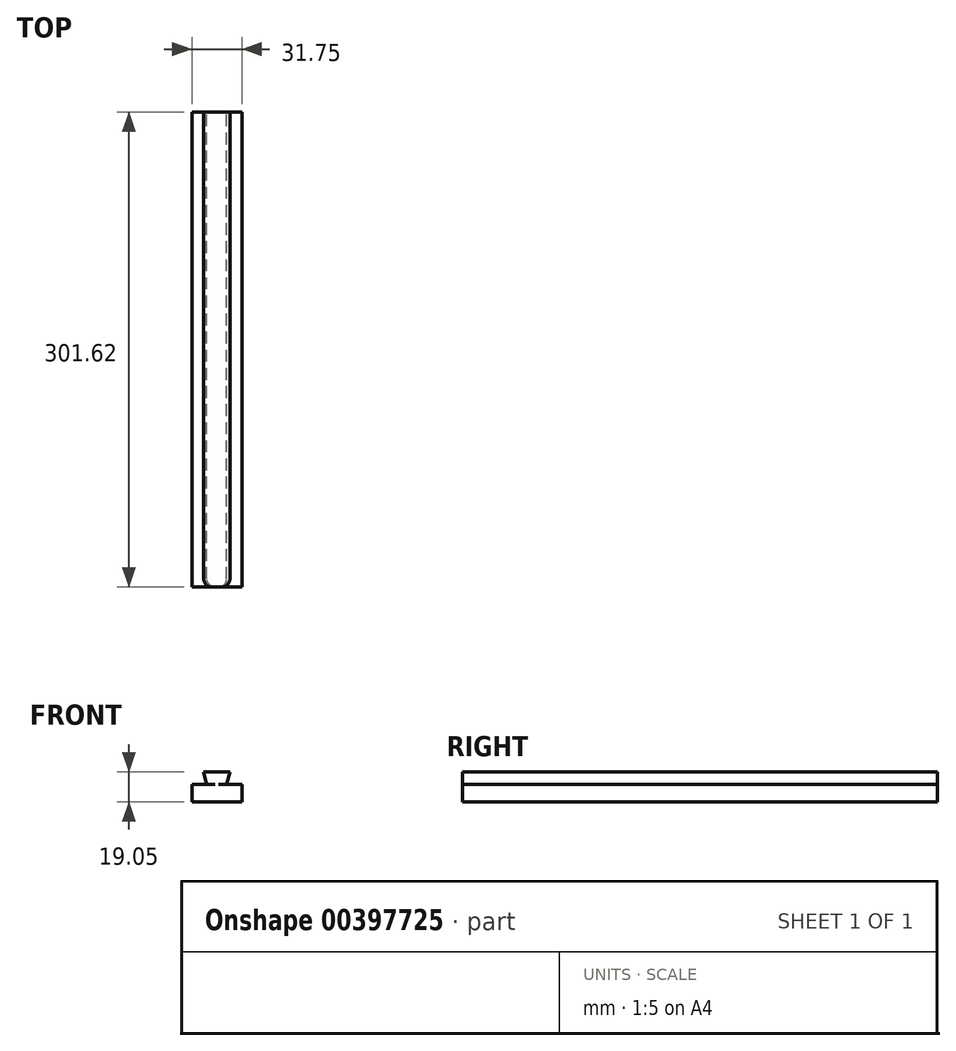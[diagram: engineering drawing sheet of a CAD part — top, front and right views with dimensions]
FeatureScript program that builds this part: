
annotation { "Feature Type Name" : "Feature", "Feature Type Description" : "" }
export const myFeature = defineFeature(function(context is Context, id is Id, definition is map)
    precondition{}
    {
        {
            var Q0;
            Q0=qCreatedBy(makeId("Front.planeOp"),FACE);
            var sketch = newSketch(context, id + "F0", { "sketchPlane" : qUnion([Q0])});
            skLineSegment(sketch, "E0.bottom", {"start": v(0, 0) * mm, "end": v(31.75, 0) * mm});
            skLineSegment(sketch, "E0.top", {"start": v(7.55, 19.05) * mm, "end": v(24.2, 19.05) * mm});
            skLineSegment(sketch, "E0.left", {"start": v(0, 0) * mm, "end": v(0, 11.11) * mm});
            skLineSegment(sketch, "E0.right", {"start": v(31.75, 0) * mm, "end": v(31.75, 11.11) * mm});
            skLineSegment(sketch, "E1", {"start": v(7.55, 19.05) * mm, "end": v(9.52, 11.11) * mm});
            skLineSegment(sketch, "E2", {"start": v(9.52, 11.11) * mm, "end": v(0, 11.11) * mm});
            skLineSegment(sketch, "E3", {"start": v(24.2, 19.05) * mm, "end": v(22.23, 11.11) * mm});
            skLineSegment(sketch, "E4", {"start": v(22.23, 11.11) * mm, "end": v(31.75, 11.11) * mm});
            skLineSegment(sketch, "E5", {"start": v(9.52, 11.11) * mm, "end": v(22.23, 11.11) * mm, "construction": true});
            skSolve(sketch);
        }
        {
            var Q0;
            Q0=makeQuery(id+"F0.imprint","IMPRINT",FACE,{"disambiguationData":[TD([[makeQuery(id+"F0.imprint","IMPRINT",EDGE,{"derivedFrom":sQuery(id+"F0.wireOp",EDGE,"E0.bottom")}),1.0]])]});
            extrude(context, id + "F1", {"entities" : qUnion([Q0]), "depth" : 301.62 * mm});
        }
        {
            var Q0;
            Q0=makeQuery(id+"F1.opExtrude","CAP_EDGE",EDGE,{"disambiguationData":[OSD([sQuery(id+"F0.wireOp",EDGE,"E3")])],"isStart":false});
            var Q1;
            Q1=makeQuery(id+"F1.opExtrude","CAP_EDGE",EDGE,{"disambiguationData":[OSD([sQuery(id+"F0.wireOp",EDGE,"E1")])],"isStart":false});
            fillet(context, id + "F2", {"entities" : qUnion([Q0, Q1]), "radius" : 5.08 * mm, "tangentPropagation" : true, "allowEdgeOverflow" : false});
        }
    });
